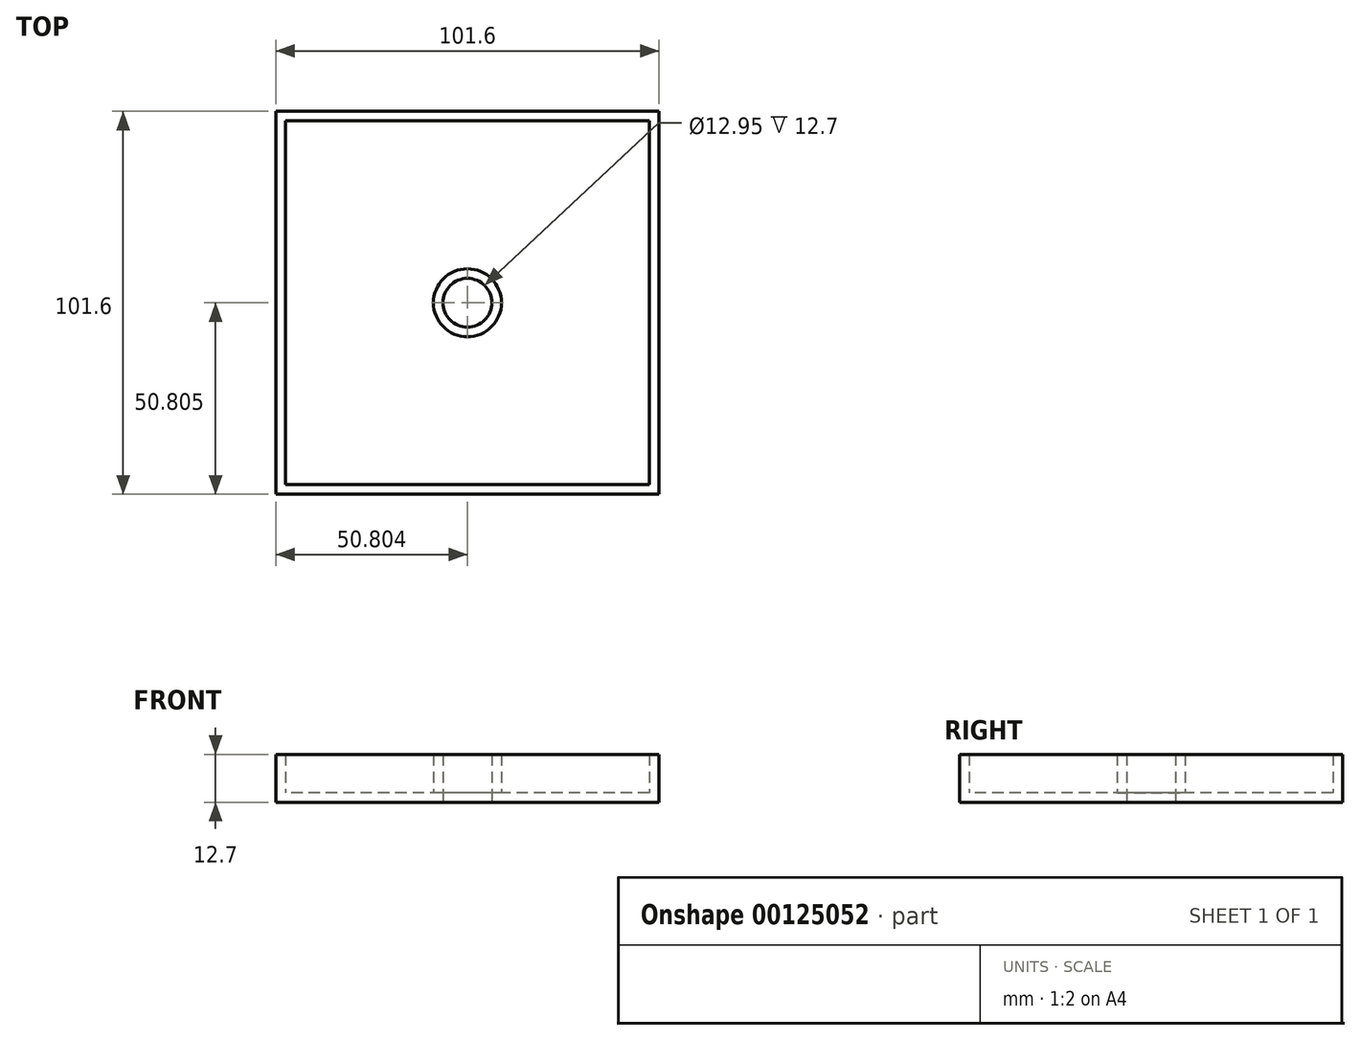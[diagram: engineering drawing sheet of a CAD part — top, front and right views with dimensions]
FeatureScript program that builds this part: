
annotation { "Feature Type Name" : "Feature", "Feature Type Description" : "" }
export const myFeature = defineFeature(function(context is Context, id is Id, definition is map)
    precondition{}
    {
        {
            var Q0;
            Q0=qCreatedBy(makeId("Top.planeOp"),FACE);
            var sketch = newSketch(context, id + "F0", { "sketchPlane" : qUnion([Q0])});
            skLineSegment(sketch, "E0", {"start": v(-50.72, 69.08) * mm, "end": v(-50.72, -32.52) * mm});
            skLineSegment(sketch, "E1", {"start": v(-50.72, -32.52) * mm, "end": v(50.88, -32.52) * mm});
            skLineSegment(sketch, "E2", {"start": v(50.88, -32.52) * mm, "end": v(50.88, 69.08) * mm});
            skLineSegment(sketch, "E3", {"start": v(50.88, 69.08) * mm, "end": v(-50.72, 69.08) * mm});
            skCircle(sketch, "E4", {"center": v(0.08, 18.28) * mm, "radius": 6.48 * mm});
            skPoint(sketch, "E4.centerSnap0", {"position": v(-50.72, 18.28) * mm});
            skPoint(sketch, "E4.centerSnap1", {"position": v(0.08, 69.08) * mm});
            skSolve(sketch);
        }
        {
            var Q0;
            Q0 = qSketchRegion(id + "F0", true);
            extrude(context, id + "F1", {"entities" : qUnion([Q0]), "depth" : 12.7 * mm});
        }
        {
            var Q0;
            Q0=makeQuery(id+"F1.opExtrude","CAP_FACE",FACE,{"disambiguationData":[OSD([sQuery(id+"F0.wireOp",EDGE,"E0"),sQuery(id+"F0.wireOp",EDGE,"E1"),sQuery(id+"F0.wireOp",EDGE,"E2"),sQuery(id+"F0.wireOp",EDGE,"E3"),sQuery(id+"F0.wireOp",EDGE,"E4")])],"isStart":false});
            shell(context, id + "F2", {"entities" : qUnion([Q0]), "thickness" : 2.54 * mm});
        }
    });
